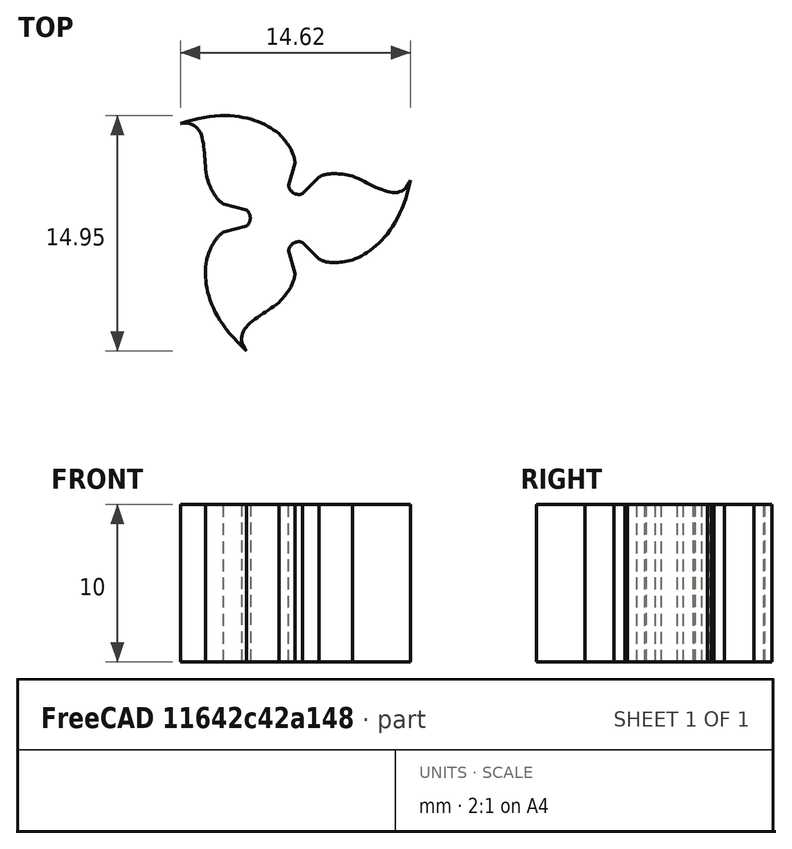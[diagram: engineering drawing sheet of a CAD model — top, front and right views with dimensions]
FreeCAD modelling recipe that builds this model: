
FCSTD DOCUMENT  (FreeCAD 1.0R39109 (Git))
Label: teatGG
License: All rights reserved
LicenseURL: https://en.wikipedia.org/wiki/All_rights_reserved
objects: Part::Part2DObjectPython×1, PartDesign::Pad×1, PartDesign::Body×1
note: 5 computed .brp shape members not serialized (recipe doc carries the construction recipe); baked Part::Feature solids carry a one-line shape summary decoded from their .brp

FEATURE [Part::Part2DObjectPython] InvoluteGear  # Draft 2D object (typed FeaturePython)
  AddendumCoefficient = 0.85
  DedendumCoefficient = 2
  ExternalGear = true
  HighPrecision = true
  Modules = 2.5
  NumberOfTeeth = 3
  PressureAngle = 20
  ProfileShiftCoefficient = 1.1
  RootFilletCoefficient = 0.26
FEATURE [PartDesign::Pad] Pad
  Direction = (0,0,1)
  Length = 10
  Length2 = 10
  Profile = -> InvoluteGear
  ReferenceAxis = -> InvoluteGear [N_Axis]
  Refine = true
  Suppressed = false
  Type = 0
FEATURE [PartDesign::Body] Body
  AllowCompound = false
  Group = -> [InvoluteGear,Pad]
  Origin = -> Origin
  Tip = -> Pad
